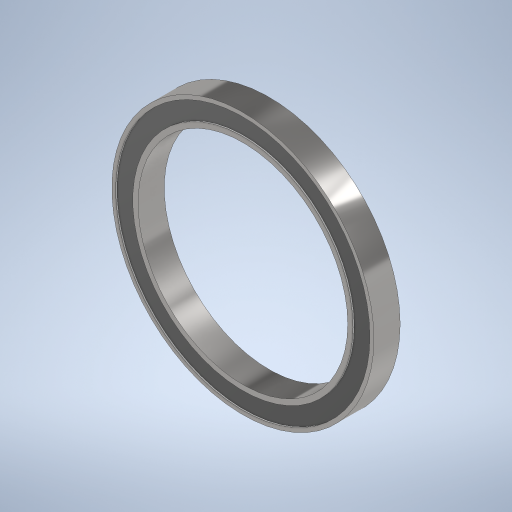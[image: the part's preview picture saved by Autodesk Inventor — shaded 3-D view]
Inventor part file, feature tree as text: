
AUTODESK INVENTOR PART (.ipt)
format: ipt  version: 2023 (Build 270158000, 158)  size: 294,400 bytes
history: native  units: mm
features: extrude x3, sketch x3, projected_geometry x1
ambient origin geometry x8: Origin, YZ Plane, XZ Plane, XY Plane, X Axis, Y Axis, Z Axis, Center Point
bodies: Solid1 (feature_tree)
feature tree (7):
  extrude  "Extrusion1"  Depth=99.95mm
  extrude  "Extrusion2"  Depth=10.0mm
  extrude  "Extrusion3"  Depth=0.5mm TaperAngle=0.0deg
  sketch  "Sketch1"  dims[d0=80.0mm d1=99.95mm]
  sketch  "Sketch2"  dims[d2=10.0mm d3=0.0mm d4=1.5mm]
  projected_geometry  "Projected Loop1"
  sketch  "Sketch3"  dims[d5=2.0mm d6=0.5mm d7=0.0mm d8=0.5mm d9=0.0mm]
